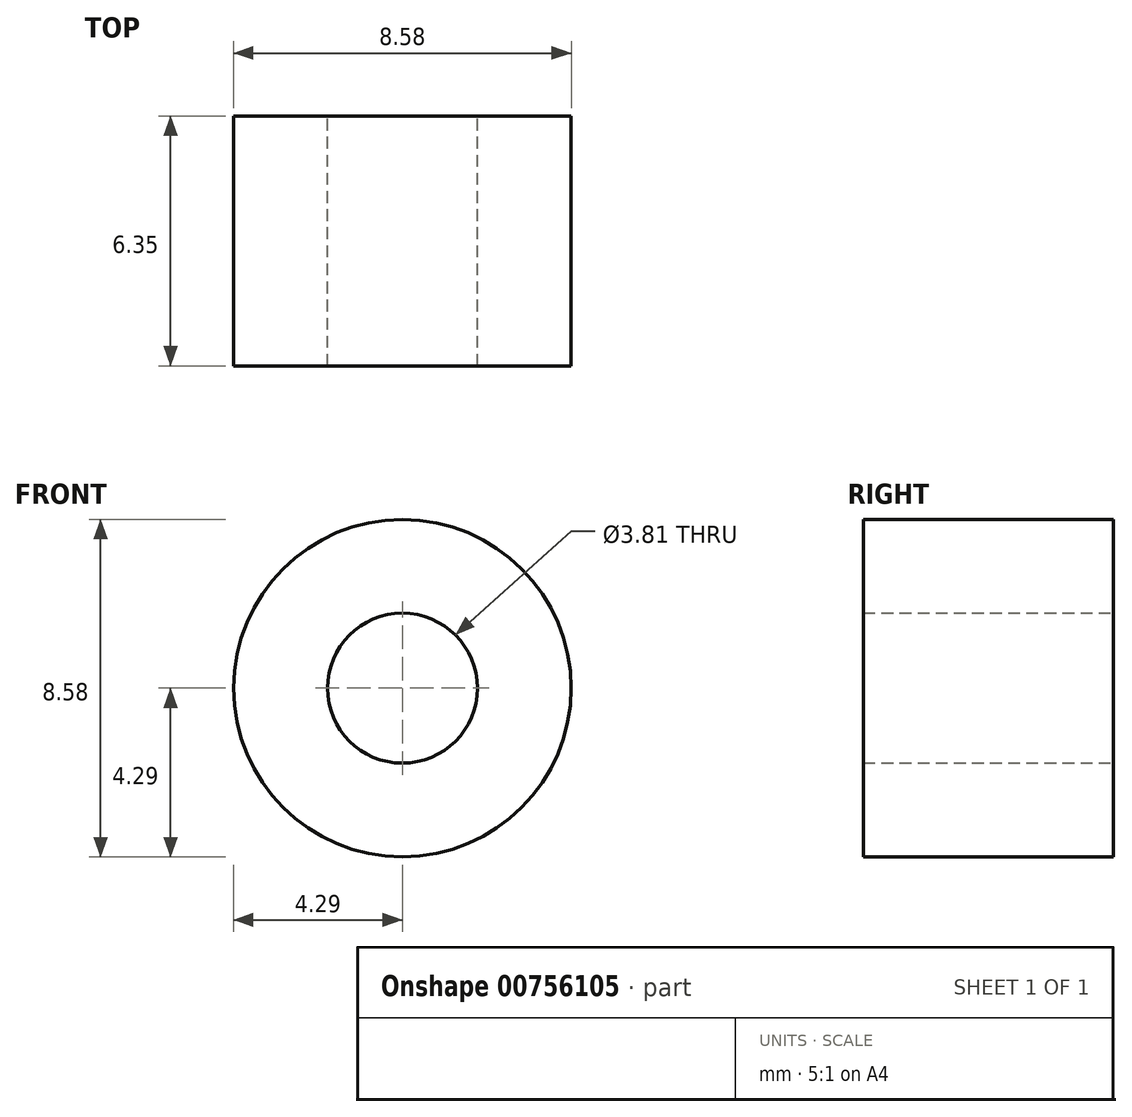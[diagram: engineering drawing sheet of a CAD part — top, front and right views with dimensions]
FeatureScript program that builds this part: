
annotation { "Feature Type Name" : "Feature", "Feature Type Description" : "" }
export const myFeature = defineFeature(function(context is Context, id is Id, definition is map)
    precondition{}
    {
        {
            var Q0;
            Q0=qCreatedBy(makeId("Front.planeOp"),FACE);
            var sketch = newSketch(context, id + "F0", { "sketchPlane" : qUnion([Q0])});
            skCircle(sketch, "E0", {"center": v(0, 0) * mm, "radius": 1.9 * mm});
            skCircle(sketch, "E1", {"center": v(0, 0) * mm, "radius": 4.29 * mm});
            skSolve(sketch);
        }
        {
            var Q0;
            Q0 = qSketchRegion(id + "F0", true);
            extrude(context, id + "F1", {"entities" : qUnion([Q0]), "depth" : 6.35 * mm, "offsetDistance" : 25.4 * mm});
        }
    });
